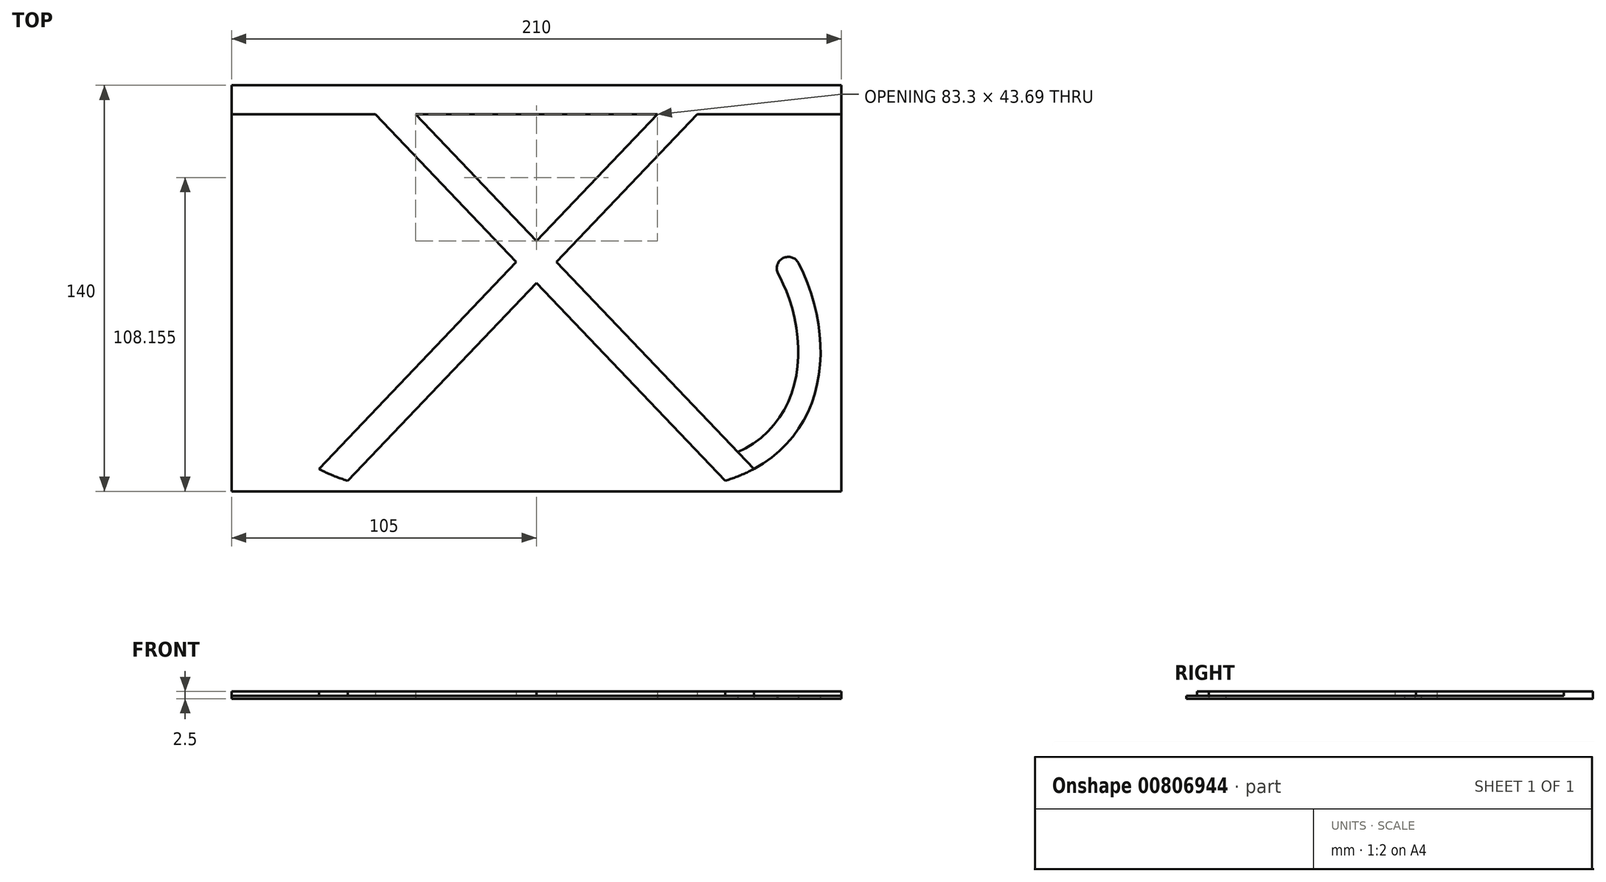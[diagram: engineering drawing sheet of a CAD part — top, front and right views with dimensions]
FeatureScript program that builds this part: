
annotation { "Feature Type Name" : "Feature", "Feature Type Description" : "" }
export const myFeature = defineFeature(function(context is Context, id is Id, definition is map)
    precondition{}
    {
        {
            var Q0;
            Q0=qCreatedBy(makeId("Top.planeOp"),FACE);
            var sketch = newSketch(context, id + "F0", { "sketchPlane" : qUnion([Q0])});
            skLineSegment(sketch, "E0.bottom", {"start": v(-105, 68.18) * mm, "end": v(105, 68.18) * mm});
            skLineSegment(sketch, "E0.top", {"start": v(-105, -71.82) * mm, "end": v(105, -71.82) * mm});
            skLineSegment(sketch, "E0.left", {"start": v(-105, 68.18) * mm, "end": v(-105, -71.82) * mm});
            skLineSegment(sketch, "E0.right", {"start": v(105, 68.18) * mm, "end": v(105, -71.82) * mm});
            skPoint(sketch, "E0.middle", {"position": v(0, -1.82) * mm});
            skPoint(sketch, "E1", {"position": v(-65, 68.18) * mm});
            skPoint(sketch, "E2.MirrorP", {"position": v(65, 68.18) * mm});
            skPoint(sketch, "E3.MirrorP", {"position": v(65, -68.18) * mm});
            skPoint(sketch, "E4.MirrorP", {"position": v(-65, -68.18) * mm});
            skLineSegment(sketch, "E5", {"start": v(-65, 68.18) * mm, "end": v(65, -68.18) * mm});
            skLineSegment(sketch, "E6", {"start": v(65, 68.18) * mm, "end": v(-65, -68.18) * mm});
            skLineSegment(sketch, "E7.0", {"start": v(57.76, 75.08) * mm, "end": v(-72.24, -61.28) * mm});
            skLineSegment(sketch, "E8.0", {"start": v(-57.76, 75.08) * mm, "end": v(72.24, -61.28) * mm});
            skPoint(sketch, "E9", {"position": v(-105, 58.18) * mm});
            skLineSegment(sketch, "E10", {"start": v(-105, 58.18) * mm, "end": v(105, 58.18) * mm});
            skLineSegment(sketch, "E11", {"start": v(-65, -68.18) * mm, "end": v(-72.24, -61.28) * mm});
            skLineSegment(sketch, "E12", {"start": v(65, -68.18) * mm, "end": v(72.24, -61.28) * mm});
            skPoint(sketch, "E13", {"position": v(-90.32, 6.9) * mm});
            skPoint(sketch, "E13.positionSnap0", {"position": v(-7.24, 6.9) * mm});
            skPoint(sketch, "E14.MirrorP", {"position": v(90.32, 6.9) * mm});
            skFitSpline(sketch, "E15", {"points": [v(-65, -68.18) * mm, v(-90.32, 6.9) * mm], "startDerivative": vector(-102.93, 30.88) * mm, "endDerivative": vector(44.03, 87.52) * mm});
            skFitSpline(sketch, "E16.0", {"points": [v(-62.7, -60.51) * mm, v(-66.41, -59.4) * mm, v(-72.88, -56.55) * mm, v(-80.12, -50.82) * mm, v(-85.3, -43.85) * mm, v(-88.63, -35.73) * mm, v(-90.13, -26.6) * mm, v(-89.76, -16.78) * mm, v(-87.52, -6.65) * mm, v(-84.82, 0.04) * mm, v(-83.18, 3.3) * mm]});
            skArc(sketch, "E17", {"start": v(-83.18, 3.3) * mm, "mid": v(-85, 8.58) * mm, "end": v(-90.32, 6.9) * mm});
            skFitSpline(sketch, "E18.MirrorCS", {"points": [v(65, -68.18) * mm, v(90.32, 6.9) * mm], "startDerivative": vector(102.93, 30.88) * mm, "endDerivative": vector(-44.03, 87.52) * mm});
            skArc(sketch, "E19.MirrorCS", {"start": v(83.18, 3.3) * mm, "mid": v(85, 8.58) * mm, "end": v(90.32, 6.9) * mm});
            skFitSpline(sketch, "E20.0", {"points": [v(62.7, -60.51) * mm, v(66.41, -59.4) * mm, v(72.88, -56.55) * mm, v(80.12, -50.82) * mm, v(85.3, -43.85) * mm, v(88.63, -35.73) * mm, v(90.13, -26.6) * mm, v(89.76, -16.78) * mm, v(87.52, -6.65) * mm, v(84.82, 0.04) * mm, v(83.18, 3.3) * mm]});
            skLineSegment(sketch, "E21", {"start": v(-72.24, -61.28) * mm, "end": v(-74.93, -64.1) * mm});
            skLineSegment(sketch, "E22", {"start": v(72.24, -61.28) * mm, "end": v(74.93, -64.1) * mm});
            skSolve(sketch);
        }
        {
            var Q0;
            {var subQ0=sQuery(id+"F0.wireOp",EDGE,"E8.0");var subQ1=sQuery(id+"F0.wireOp",EDGE,"E0.bottom");var subQ2=makeQuery(id+"F0.imprint","INTERSECT",VERTEX,{"derivedFrom":[subQ1,subQ0]});Q0=makeQuery(id+"F0.imprint","IMPRINT",FACE,{"disambiguationData":[TD([[makeQuery(id+"F0.imprint","IMPRINT",EDGE,{"disambiguationData":[TD([[subQ2,-1.0]])],"derivedFrom":subQ1}),-1.0]])]});}
            var Q1;
            {var subQ0=sQuery(id+"F0.wireOp",EDGE,"E10");var subQ1=sQuery(id+"F0.wireOp",EDGE,"E6");var subQ2=makeQuery(id+"F0.imprint","INTERSECT",VERTEX,{"derivedFrom":[subQ1,subQ0]});Q1=makeQuery(id+"F0.imprint","IMPRINT",FACE,{"disambiguationData":[TD([[makeQuery(id+"F0.imprint","IMPRINT",EDGE,{"disambiguationData":[TD([[subQ2,-1.0]])],"derivedFrom":subQ1}),-1.0]])]});}
            var Q2;
            {var subQ0=sQuery(id+"F0.wireOp",EDGE,"E6");var subQ1=sQuery(id+"F0.wireOp",EDGE,"E0.bottom");var subQ2=makeQuery(id+"F0.imprint","INTERSECT",VERTEX,{"derivedFrom":[subQ1,subQ0]});Q2=makeQuery(id+"F0.imprint","IMPRINT",FACE,{"disambiguationData":[TD([[makeQuery(id+"F0.imprint","IMPRINT",EDGE,{"disambiguationData":[TD([[subQ2,1.0]])],"derivedFrom":subQ1}),-1.0]])]});}
            var Q3;
            {var subQ0=sQuery(id+"F0.wireOp",EDGE,"E0.right");var subQ1=sQuery(id+"F0.wireOp",EDGE,"E0.bottom");var subQ2=makeQuery(id+"F0.imprint","INTERSECT",VERTEX,{"derivedFrom":[subQ1,subQ0]});Q3=makeQuery(id+"F0.imprint","IMPRINT",FACE,{"disambiguationData":[TD([[makeQuery(id+"F0.imprint","IMPRINT",EDGE,{"disambiguationData":[TD([[subQ2,1.0]])],"derivedFrom":subQ1}),-1.0]])]});}
            var Q4;
            {var subQ0=sQuery(id+"F0.wireOp",EDGE,"E7.0");var subQ1=sQuery(id+"F0.wireOp",EDGE,"E5");var subQ2=makeQuery(id+"F0.imprint","INTERSECT",VERTEX,{"derivedFrom":[subQ1,subQ0]});Q4=makeQuery(id+"F0.imprint","IMPRINT",FACE,{"disambiguationData":[TD([[makeQuery(id+"F0.imprint","IMPRINT",EDGE,{"disambiguationData":[TD([[subQ2,-1.0]])],"derivedFrom":subQ1}),1.0]])]});}
            var Q5;
            {var subQ0=sQuery(id+"F0.wireOp",EDGE,"E10");var subQ1=sQuery(id+"F0.wireOp",EDGE,"E5");var subQ2=makeQuery(id+"F0.imprint","INTERSECT",VERTEX,{"derivedFrom":[subQ1,subQ0]});Q5=makeQuery(id+"F0.imprint","IMPRINT",FACE,{"disambiguationData":[TD([[makeQuery(id+"F0.imprint","IMPRINT",EDGE,{"disambiguationData":[TD([[subQ2,-1.0]])],"derivedFrom":subQ1}),1.0]])]});}
            var Q6;
            {var subQ0=sQuery(id+"F0.wireOp",EDGE,"E0.left");var subQ1=sQuery(id+"F0.wireOp",EDGE,"E0.bottom");var subQ2=makeQuery(id+"F0.imprint","INTERSECT",VERTEX,{"derivedFrom":[subQ1,subQ0]});Q6=makeQuery(id+"F0.imprint","IMPRINT",FACE,{"disambiguationData":[TD([[makeQuery(id+"F0.imprint","IMPRINT",EDGE,{"disambiguationData":[TD([[subQ2,-1.0]])],"derivedFrom":subQ1}),-1.0]])]});}
            var Q7;
            {var subQ0=sQuery(id+"F0.wireOp",EDGE,"E5");var subQ1=sQuery(id+"F0.wireOp",EDGE,"E0.bottom");var subQ2=makeQuery(id+"F0.imprint","INTERSECT",VERTEX,{"derivedFrom":[subQ1,subQ0]});Q7=makeQuery(id+"F0.imprint","IMPRINT",FACE,{"disambiguationData":[TD([[makeQuery(id+"F0.imprint","IMPRINT",EDGE,{"disambiguationData":[TD([[subQ2,-1.0]])],"derivedFrom":subQ1}),-1.0]])]});}
            var Q8;
            {var subQ4=sQuery(id+"F0.wireOp",EDGE,"E11");Q8=makeQuery(id+"F0.imprint","IMPRINT",FACE,{"disambiguationData":[TD([[makeQuery(id+"F0.imprint","IMPRINT",EDGE,{"derivedFrom":subQ4}),-1.0]])]});}
            var Q9;
            {var subQ0=sQuery(id+"F0.wireOp",EDGE,"E12");Q9=makeQuery(id+"F0.imprint","IMPRINT",FACE,{"disambiguationData":[TD([[makeQuery(id+"F0.imprint","IMPRINT",EDGE,{"derivedFrom":subQ0}),1.0]])]});}
            var Q10;
            {var subQ0=sQuery(id+"F0.wireOp",EDGE,"E12");Q10=makeQuery(id+"F0.imprint","IMPRINT",FACE,{"disambiguationData":[TD([[makeQuery(id+"F0.imprint","IMPRINT",EDGE,{"derivedFrom":subQ0}),-1.0]])]});}
            var Q11;
            {var subQ0=sQuery(id+"F0.wireOp",EDGE,"E11");Q11=makeQuery(id+"F0.imprint","IMPRINT",FACE,{"disambiguationData":[TD([[makeQuery(id+"F0.imprint","IMPRINT",EDGE,{"derivedFrom":subQ0}),1.0]])]});}
            extrude(context, id + "F1", {"entities" : qUnion([Q0, Q1, Q2, Q3, Q4, Q5, Q6, Q7, Q8, Q9, Q10, Q11]), "depth" : 2.5 * mm, "offsetDistance" : 25 * mm});
        }
        {
            var Q0;
            {var subQ0=sQuery(id+"F0.wireOp",EDGE,"E17");Q0=makeQuery(id+"F0.imprint","IMPRINT",FACE,{"disambiguationData":[TD([[makeQuery(id+"F0.imprint","IMPRINT",EDGE,{"derivedFrom":subQ0}),1.0]])]});}
            var Q1;
            {var subQ0=sQuery(id+"F0.wireOp",EDGE,"E19.MirrorCS");Q1=makeQuery(id+"F0.imprint","IMPRINT",FACE,{"disambiguationData":[TD([[makeQuery(id+"F0.imprint","IMPRINT",EDGE,{"derivedFrom":subQ0}),-1.0]])]});}
            extrude(context, id + "F2", {"entities" : qUnion([Q0, Q1]), "operationType" : NewBodyOperationType.ADD, "depth" : 1 * mm, "offsetDistance" : 25 * mm});
        }
    });
